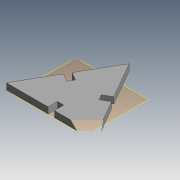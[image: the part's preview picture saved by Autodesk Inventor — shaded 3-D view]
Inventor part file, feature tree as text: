
AUTODESK INVENTOR PART (.ipt)
format: ipt  version: 2014 SP1 (Build 180222100, 222)  size: 136,704 bytes
history: native  units: in
note: dims shown in document units (in); Inventor stores cm internally (conversion verified against a paired STEP export)
features: fillet x2, plane x1, extrude x1, pattern_circular x1, sketch x1
ambient origin geometry x8: Origin, YZ Plane, XZ Plane, XY Plane, X Axis, Y Axis, Z Axis, Center Point
bodies: Body1 (feature_tree)
feature tree (6):
  plane  "Work Plane1"
  extrude  "Extrusion2"  Depth=0.1181in
  fillet  "Fillet1"  Radius=0.4075in
  fillet  "Fillet2"  Radius=0.2228in
  pattern_circular  "Circular Pattern1"  [2 undecoded]
  sketch  "Sketch1"  dims[d5=60.0deg d6=120.0deg d34=1.5748in d35=0.4075in d40=0.2228in d41=0.0in d45=0.1181in d47=0.315in d48=0.1181in d52=1.1811in d54=360.0deg d57=0.1181in d58=0.1181in d59=1.1811in d60=360.0deg]
note: 2 required parameter values undecoded (feature->parameter linkage not recoverable at this tier; creation-order binding heuristic only, values carry confidence <= 0.55)
